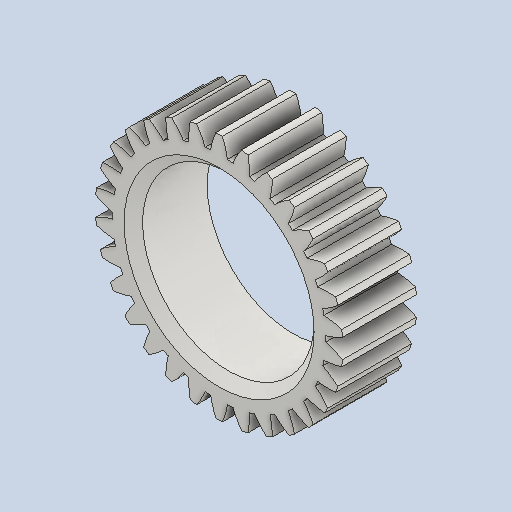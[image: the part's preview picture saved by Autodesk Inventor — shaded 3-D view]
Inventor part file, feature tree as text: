
AUTODESK INVENTOR PART (.ipt)
format: ipt  version: 2022 (Build 260153000, 153)  size: 359,936 bytes
history: native  units: in
note: dims shown in document units (in); Inventor stores cm internally (conversion verified against a paired STEP export)
features: other x12, plane x4, sketch x3
ambient origin geometry x8: Origin, YZ Plane, XZ Plane, XY Plane, X Axis, Y Axis, Z Axis, Center Point
bodies: Solid1 (feature_tree)
feature tree (19):
  other  "Spur Gear13_MIR.ipt"
  other  "Solid1::Spur Gear13_MIR.ipt"
  other  "TaggingFeature1"
  sketch  "Sketch1"  dims[d0=0.3937in]
  sketch  "Sketch2"  dims[d9=0.0in d14=0.0in d15=1.0in d16=0.0in d17=0.0in d18=0.0in d19=1.0in]
  sketch  "Sketch3"
  plane  "XZ Plane_1"
  plane  "Work Plane2"
  plane  "Work Plane3"
  plane  "Work Plane4"
  other  "Srf1"
  other  "Srf1::Derived"
  other  "Start plane iMate"
  other  "Distance iMate"
  other  "Position iMate"
  other  "Mesh iMate"
  other  "Axis iMate"
  other  "Mesh iMate2"
  other  "Align iMate"
